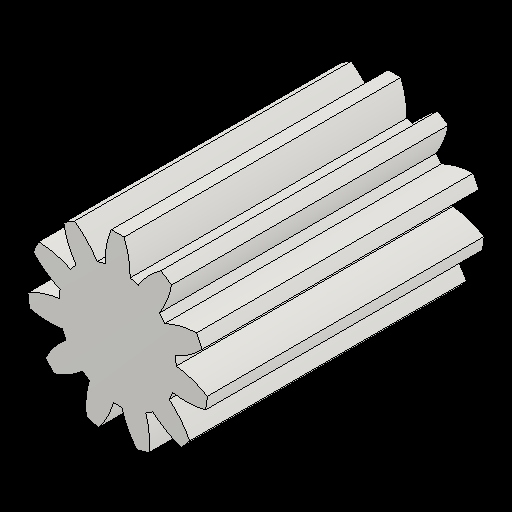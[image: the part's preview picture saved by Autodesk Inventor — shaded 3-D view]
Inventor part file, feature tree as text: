
AUTODESK INVENTOR PART (.ipt)
format: ipt  version: 2023.2 (Build 272271030, 271C)  size: 190,464 bytes
history: native  units: mm (DEFAULTED — no unit token found)
features: plane x3, other x3, sketch x2, extrude x1
ambient origin geometry x8: Origin, YZ Plane, XZ Plane, XY Plane, X Axis, Y Axis, Z Axis, Center Point
bodies: Solid1 (feature_tree)
feature tree (9):
  extrude  "Extrusion1"  Depth=20.0mm TaperAngle=0.0deg
  plane  "Work Plane2"
  plane  "Work Plane8"
  plane  "Work Plane9"
  other  "Spur Gear"
  sketch  "Sketch1"  dims[d0=13.0mm d1=20.0mm d2=0.0mm]
  sketch  "Sketch2"  dims[d3=11.0mm d4=10.0mm d5=0.0mm d16=11.0mm d17=0.0mm d34=2.855993mm d39=0.0mm d41=0.0mm d43=11.0mm d46=11.0mm d47=0.0mm d48=0.0mm]
  other  "Srf1"
  other  "Pitch Diameter"
